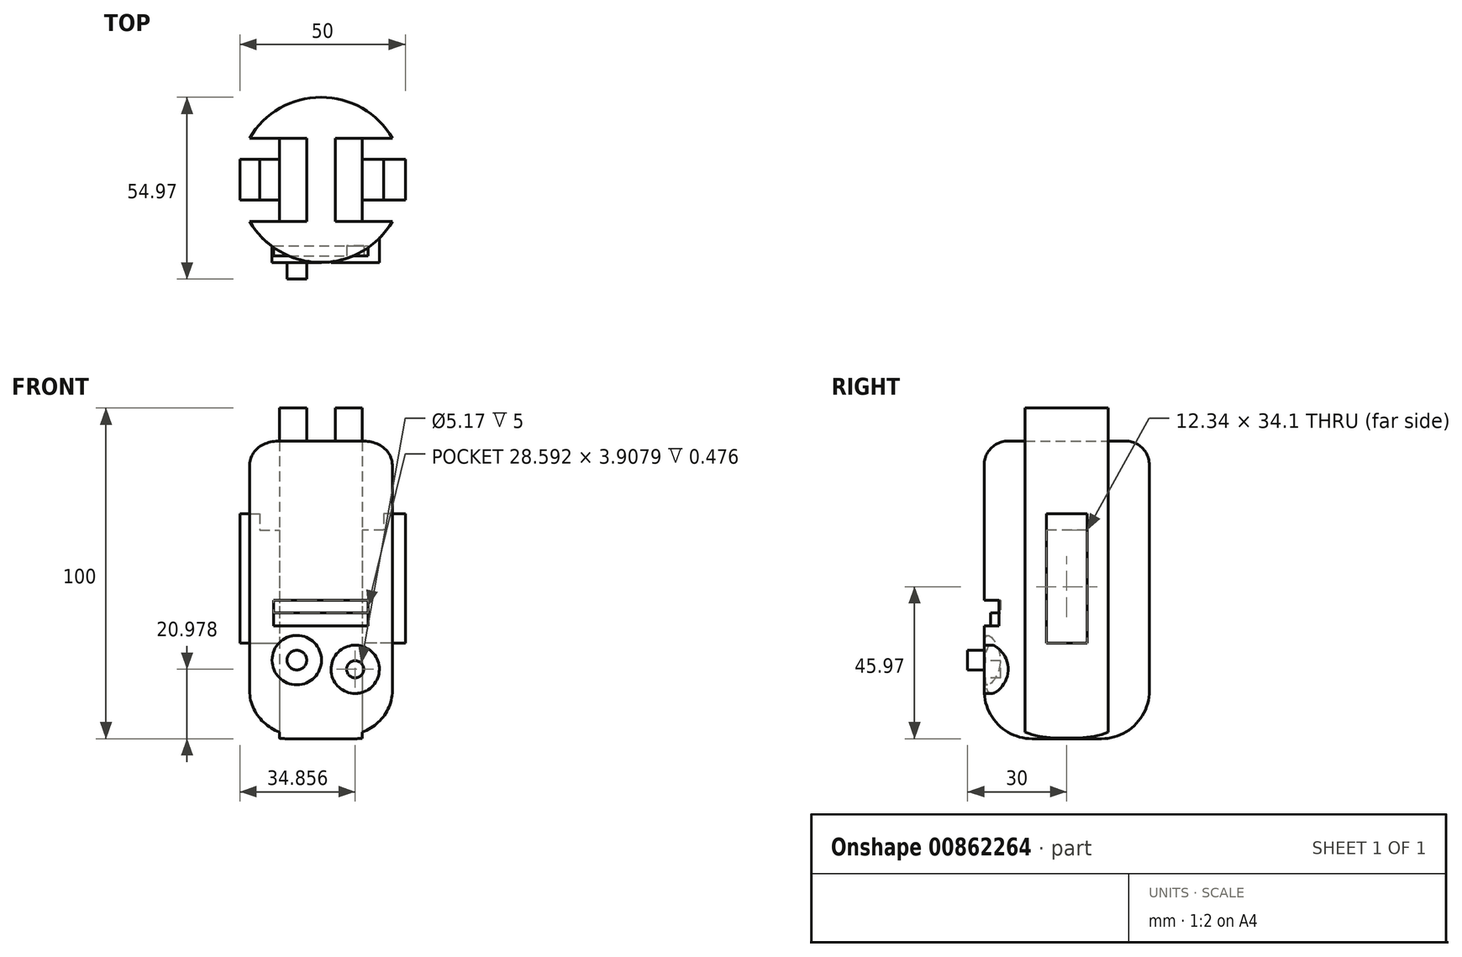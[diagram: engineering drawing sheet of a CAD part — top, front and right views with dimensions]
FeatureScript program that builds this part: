
annotation { "Feature Type Name" : "Feature", "Feature Type Description" : "" }
export const myFeature = defineFeature(function(context is Context, id is Id, definition is map)
    precondition{}
    {
        {
            var Q0;
            Q0=qCreatedBy(makeId("Top.planeOp"),FACE);
            var sketch = newSketch(context, id + "F0", { "sketchPlane" : qUnion([Q0])});
            skCircle(sketch, "E0", {"center": v(0, 0) * mm, "radius": 24.97 * mm});
            skSolve(sketch);
        }
        {
            var Q0;
            Q0=makeQuery(id+"F0.imprint","IMPRINT",FACE,{"disambiguationData":[TD([[makeQuery(id+"F0.imprint","IMPRINT",EDGE,{"derivedFrom":sQuery(id+"F0.wireOp",EDGE,"E0")}),1.0]])]});
            extrude(context, id + "F1", {"entities" : qUnion([Q0]), "depth" : 80 * mm, "offsetDistance" : 25 * mm});
        }
        {
            var Q0;
            Q0=makeQuery(id+"F1.opExtrude","CAP_FACE",FACE,{"disambiguationData":[OSD([sQuery(id+"F0.wireOp",EDGE,"E0")])],"isStart":false});
            fillet(context, id + "F2", {"entities" : qUnion([Q0]), "radius" : 7.24 * mm, "tangentPropagation" : true, "allowEdgeOverflow" : false});
        }
        {
            var Q0;
            Q0=makeQuery(id+"F1.opExtrude","CAP_FACE",FACE,{"disambiguationData":[OSD([sQuery(id+"F0.wireOp",EDGE,"E0")])],"isStart":false});
            var sketch = newSketch(context, id + "F3", { "sketchPlane" : qUnion([Q0])});
            skLineSegment(sketch, "E1.bottom", {"start": v(12.5, -12.57) * mm, "end": v(-12.5, -12.57) * mm});
            skLineSegment(sketch, "E1.top", {"start": v(12.5, 12.57) * mm, "end": v(-12.5, 12.57) * mm});
            skLineSegment(sketch, "E1.left", {"start": v(12.5, -12.57) * mm, "end": v(12.5, 12.57) * mm});
            skLineSegment(sketch, "E1.right", {"start": v(-12.5, -12.57) * mm, "end": v(-12.5, 12.57) * mm});
            skPoint(sketch, "E1.middle", {"position": v(0, 0) * mm});
            skSolve(sketch);
        }
        {
            var Q0;
            Q0 = qSketchRegion(id + "F3", true);
            extrude(context, id + "F4", {"entities" : qUnion([Q0]), "operationType" : NewBodyOperationType.ADD, "depth" : 10 * mm, "offsetDistance" : 25 * mm});
        }
        {
            var Q0;
            Q0=makeQuery(id+"F4.opExtrude","CAP_FACE",FACE,{"disambiguationData":[OSD([sQuery(id+"F3.wireOp",EDGE,"E1.bottom"),sQuery(id+"F3.wireOp",EDGE,"E1.top"),sQuery(id+"F3.wireOp",EDGE,"E1.left"),sQuery(id+"F3.wireOp",EDGE,"E1.right")])],"isStart":false});
            var sketch = newSketch(context, id + "F5", { "sketchPlane" : qUnion([Q0])});
            skLineSegment(sketch, "E2.bottom", {"start": v(4.3, -21.17) * mm, "end": v(-4.3, -21.17) * mm});
            skLineSegment(sketch, "E2.top", {"start": v(4.3, 21.17) * mm, "end": v(-4.3, 21.17) * mm});
            skLineSegment(sketch, "E2.left", {"start": v(4.3, -21.17) * mm, "end": v(4.3, 21.17) * mm});
            skLineSegment(sketch, "E2.right", {"start": v(-4.3, -21.17) * mm, "end": v(-4.3, 21.17) * mm});
            skPoint(sketch, "E2.middle", {"position": v(0, 0) * mm});
            skSolve(sketch);
        }
        {
            var Q0;
            Q0 = qSketchRegion(id + "F5", true);
            extrude(context, id + "F6", {"entities" : qUnion([Q0]), "operationType" : NewBodyOperationType.REMOVE, "oppositeDirection" : true, "depth" : 10 * mm, "offsetDistance" : 25 * mm});
        }
        {
            var Q0;
            Q0=makeQuery(id+"F1.opExtrude","CAP_FACE",FACE,{"disambiguationData":[OSD([sQuery(id+"F0.wireOp",EDGE,"E0")])],"isStart":true});
            var sketch = newSketch(context, id + "F7", { "sketchPlane" : qUnion([Q0])});
            skCircle(sketch, "E3", {"center": v(0, 0) * mm, "radius": 24.97 * mm});
            skSolve(sketch);
        }
        {
            var Q0;
            Q0 = qSketchRegion(id + "F7", true);
            extrude(context, id + "F8", {"entities" : qUnion([Q0]), "operationType" : NewBodyOperationType.ADD, "depth" : 10 * mm, "offsetDistance" : 25 * mm});
        }
        {
            var Q0;
            Q0=makeQuery(id+"F8.opExtrude","CAP_EDGE",EDGE,{"disambiguationData":[OSD([sQuery(id+"F7.wireOp",EDGE,"E3")])],"isStart":false});
            fillet(context, id + "F9", {"entities" : qUnion([Q0]), "radius" : 14.5 * mm, "tangentPropagation" : true, "allowEdgeOverflow" : false});
        }
        {
            var Q0;
            Q0=qCreatedBy(makeId("Front.planeOp"),FACE);
            var sketch = newSketch(context, id + "F10", { "sketchPlane" : qUnion([Q0])});
            skCircle(sketch, "E4", {"center": v(10.36, 10.98) * mm, "radius": 7.3 * mm});
            skCircle(sketch, "E5", {"center": v(-7.3, 13.75) * mm, "radius": 7.48 * mm});
            skSolve(sketch);
        }
        {
            var Q0;
            Q0=sQuery(id+"F10.wireOp",EDGE,"E5");
            extrude(context, id + "F11", {"bodyType" : ToolBodyType.SURFACE, "surfaceEntities" : qUnion([Q0]), "depth" : 25 * mm, "offsetDistance" : 25 * mm});
        }
        {
            var Q0;
            Q0 = qSketchRegion(id + "F10", true);
            extrude(context, id + "F12", {"entities" : qUnion([Q0]), "operationType" : NewBodyOperationType.ADD, "depth" : 25 * mm, "offsetDistance" : 25 * mm});
        }
        {
            var Q0;
            Q0=makeQuery(id+"F12.opExtrude","CAP_FACE",FACE,{"disambiguationData":[OSD([sQuery(id+"F10.wireOp",EDGE,"E4")])],"isStart":false});
            var sketch = newSketch(context, id + "F13", { "sketchPlane" : qUnion([Q0])});
            skCircle(sketch, "E6", {"center": v(10.36, 10.98) * mm, "radius": 2.58 * mm});
            skSolve(sketch);
        }
        {
            var Q0;
            Q0=makeQuery(id+"F13.imprint","IMPRINT",FACE,{"disambiguationData":[TD([[makeQuery(id+"F13.imprint","IMPRINT",EDGE,{"derivedFrom":sQuery(id+"F13.wireOp",EDGE,"E6")}),1.0]])]});
            extrude(context, id + "F14", {"entities" : qUnion([Q0]), "operationType" : NewBodyOperationType.REMOVE, "oppositeDirection" : true, "depth" : 5 * mm, "offsetDistance" : 25 * mm});
        }
        {
            var Q0;
            Q0=makeQuery(id+"F12.opExtrude","CAP_FACE",FACE,{"disambiguationData":[OSD([sQuery(id+"F10.wireOp",EDGE,"E5")])],"isStart":false});
            var sketch = newSketch(context, id + "F15", { "sketchPlane" : qUnion([Q0])});
            skCircle(sketch, "E7", {"center": v(-7.3, 13.75) * mm, "radius": 2.98 * mm});
            skSolve(sketch);
        }
        {
            var Q0;
            Q0=makeQuery(id+"F15.imprint","IMPRINT",FACE,{"disambiguationData":[TD([[makeQuery(id+"F15.imprint","IMPRINT",EDGE,{"derivedFrom":sQuery(id+"F15.wireOp",EDGE,"E7")}),1.0]])]});
            extrude(context, id + "F16", {"entities" : qUnion([Q0]), "operationType" : NewBodyOperationType.ADD, "depth" : 5 * mm, "offsetDistance" : 25 * mm});
        }
        {
            var Q0;
            Q0=makeQuery(id+"F12.opExtrude","CAP_FACE",FACE,{"disambiguationData":[OSD([sQuery(id+"F10.wireOp",EDGE,"E4")])],"isStart":false});
            var sketch = newSketch(context, id + "F17", { "sketchPlane" : qUnion([Q0])});
            skLineSegment(sketch, "E8.bottom", {"start": v(-14.3, 31.9) * mm, "end": v(14.3, 31.9) * mm});
            skLineSegment(sketch, "E8.top", {"start": v(-14.3, 24.08) * mm, "end": v(14.3, 24.08) * mm});
            skLineSegment(sketch, "E8.left", {"start": v(-14.3, 31.9) * mm, "end": v(-14.3, 24.08) * mm});
            skLineSegment(sketch, "E8.right", {"start": v(14.3, 31.9) * mm, "end": v(14.3, 24.08) * mm});
            skPoint(sketch, "E8.middle", {"position": v(0, 27.99) * mm});
            skSolve(sketch);
        }
        {
            var Q0;
            Q0=makeQuery(id+"F17.imprint","IMPRINT",FACE,{"disambiguationData":[TD([[makeQuery(id+"F17.imprint","IMPRINT",EDGE,{"derivedFrom":sQuery(id+"F17.wireOp",EDGE,"E8.bottom")}),-1.0]])]});
            extrude(context, id + "F18", {"entities" : qUnion([Q0]), "operationType" : NewBodyOperationType.REMOVE, "oppositeDirection" : true, "depth" : 5 * mm, "offsetDistance" : 25 * mm});
        }
        {
            var Q0;
            Q0=makeQuery(id+"F18.boolean.opBoolean","COPY",FACE,{"derivedFrom":makeQuery(id+"F18.opExtrude","CAP_FACE",FACE,{"disambiguationData":[OSD([sQuery(id+"F17.wireOp",EDGE,"E8.bottom"),sQuery(id+"F17.wireOp",EDGE,"E8.top"),sQuery(id+"F17.wireOp",EDGE,"E8.left"),sQuery(id+"F17.wireOp",EDGE,"E8.right")])],"isStart":false})});
            var sketch = newSketch(context, id + "F19", { "sketchPlane" : qUnion([Q0])});
            skLineSegment(sketch, "E9.bottom", {"start": v(14.3, 24.08) * mm, "end": v(-14.3, 24.08) * mm});
            skLineSegment(sketch, "E9.top", {"start": v(14.3, 27.99) * mm, "end": v(-14.3, 27.99) * mm});
            skLineSegment(sketch, "E9.left", {"start": v(14.3, 24.08) * mm, "end": v(14.3, 27.99) * mm});
            skLineSegment(sketch, "E9.right", {"start": v(-14.3, 24.08) * mm, "end": v(-14.3, 27.99) * mm});
            skSolve(sketch);
        }
        {
            var Q0;
            Q0=makeQuery(id+"F19.imprint","IMPRINT",FACE,{"disambiguationData":[TD([[makeQuery(id+"F19.imprint","IMPRINT",EDGE,{"derivedFrom":sQuery(id+"F19.wireOp",EDGE,"E9.bottom")}),1.0]])]});
            extrude(context, id + "F20", {"entities" : qUnion([Q0]), "operationType" : NewBodyOperationType.ADD, "depth" : 3 * mm, "offsetDistance" : 25 * mm});
        }
        {
            var Q0;
            Q0=makeQuery(id+"F4.opExtrude","SWEPT_FACE",FACE,{"disambiguationData":[OSD([sQuery(id+"F3.wireOp",EDGE,"E1.right")])]});
            var sketch = newSketch(context, id + "F21", { "sketchPlane" : qUnion([Q0])});
            skLineSegment(sketch, "E10.bottom", {"start": v(-12.57, 80) * mm, "end": v(12.57, 80) * mm});
            skLineSegment(sketch, "E10.top", {"start": v(-12.57, -80) * mm, "end": v(12.57, -80) * mm});
            skLineSegment(sketch, "E10.left", {"start": v(-12.57, 80) * mm, "end": v(-12.57, -80) * mm});
            skLineSegment(sketch, "E10.right", {"start": v(12.57, 80) * mm, "end": v(12.57, -80) * mm});
            skPoint(sketch, "E10.middle", {"position": v(0, 0) * mm});
            skSolve(sketch);
        }
        {
            var Q0;
            Q0=makeQuery(id+"F21.imprint","IMPRINT",FACE,{"disambiguationData":[TD([[makeQuery(id+"F21.imprint","IMPRINT",EDGE,{"derivedFrom":sQuery(id+"F21.wireOp",EDGE,"E10.bottom")}),1.0]])]});
            extrude(context, id + "F22", {"entities" : qUnion([Q0]), "operationType" : NewBodyOperationType.REMOVE, "depth" : 25 * mm, "offsetDistance" : 25 * mm});
        }
        {
            var Q0;
            Q0=makeQuery(id+"F4.opExtrude","SWEPT_FACE",FACE,{"disambiguationData":[OSD([sQuery(id+"F3.wireOp",EDGE,"E1.left")])]});
            var sketch = newSketch(context, id + "F23", { "sketchPlane" : qUnion([Q0])});
            skLineSegment(sketch, "E11.bottom", {"start": v(-12.57, 80) * mm, "end": v(12.57, 80) * mm});
            skLineSegment(sketch, "E11.top", {"start": v(-12.57, -80) * mm, "end": v(12.57, -80) * mm});
            skLineSegment(sketch, "E11.left", {"start": v(-12.57, 80) * mm, "end": v(-12.57, -80) * mm});
            skLineSegment(sketch, "E11.right", {"start": v(12.57, 80) * mm, "end": v(12.57, -80) * mm});
            skPoint(sketch, "E11.middle", {"position": v(0, 0) * mm});
            skSolve(sketch);
        }
        {
            var Q0;
            Q0=makeQuery(id+"F23.imprint","IMPRINT",FACE,{"disambiguationData":[TD([[makeQuery(id+"F23.imprint","IMPRINT",EDGE,{"derivedFrom":sQuery(id+"F23.wireOp",EDGE,"E11.bottom")}),-1.0]])]});
            extrude(context, id + "F24", {"entities" : qUnion([Q0]), "operationType" : NewBodyOperationType.REMOVE, "depth" : 25 * mm, "offsetDistance" : 25 * mm});
        }
        {
            var Q0;
            Q0=makeQuery(id+"F22.boolean.opBoolean","MERGE",FACE,{"derivedFrom":[makeQuery(id+"F4.opExtrude","SWEPT_FACE",FACE,{"disambiguationData":[OSD([sQuery(id+"F3.wireOp",EDGE,"E1.right")])]}),makeQuery(id+"F22.opExtrude","CAP_FACE",FACE,{"disambiguationData":[OSD([sQuery(id+"F21.wireOp",EDGE,"E10.bottom"),sQuery(id+"F21.wireOp",EDGE,"E10.top"),sQuery(id+"F21.wireOp",EDGE,"E10.left"),sQuery(id+"F21.wireOp",EDGE,"E10.right")])],"isStart":true})]});
            var sketch = newSketch(context, id + "F25", { "sketchPlane" : qUnion([Q0])});
            skLineSegment(sketch, "E12.bottom", {"start": v(-6.17, 53.02) * mm, "end": v(6.17, 53.02) * mm});
            skLineSegment(sketch, "E12.top", {"start": v(-6.17, 18.92) * mm, "end": v(6.17, 18.92) * mm});
            skLineSegment(sketch, "E12.left", {"start": v(-6.17, 53.02) * mm, "end": v(-6.17, 18.92) * mm});
            skLineSegment(sketch, "E12.right", {"start": v(6.17, 53.02) * mm, "end": v(6.17, 18.92) * mm});
            skPoint(sketch, "E12.middle", {"position": v(0, 35.97) * mm});
            skPoint(sketch, "E12.middle.positionSnap0", {"position": v(-12.57, 35.97) * mm});
            skPoint(sketch, "E12.centerSnap0", {"position": v(-12.57, 35.97) * mm});
            skSolve(sketch);
        }
        {
            var Q0;
            Q0=makeQuery(id+"F25.imprint","IMPRINT",FACE,{"disambiguationData":[TD([[makeQuery(id+"F25.imprint","IMPRINT",EDGE,{"derivedFrom":sQuery(id+"F25.wireOp",EDGE,"E12.bottom")}),-1.0]])]});
            extrude(context, id + "F26", {"entities" : qUnion([Q0]), "operationType" : NewBodyOperationType.ADD, "oppositeDirection" : true, "depth" : 38 * mm, "offsetDistance" : 25 * mm});
        }
        {
            var Q0;
            Q0 = qSketchRegion(id + "F25", true);
            extrude(context, id + "F27", {"entities" : qUnion([Q0]), "operationType" : NewBodyOperationType.ADD, "depth" : 12 * mm, "offsetDistance" : 25 * mm});
        }
        {
            var Q0;
            Q0=makeQuery(id+"F27.opExtrude","SWEPT_FACE",FACE,{"disambiguationData":[OSD([sQuery(id+"F25.wireOp",EDGE,"E12.bottom")])]});
            var sketch = newSketch(context, id + "F28", { "sketchPlane" : qUnion([Q0])});
            skLineSegment(sketch, "E13.bottom", {"start": v(-24.5, -6.17) * mm, "end": v(-18.5, -6.17) * mm});
            skLineSegment(sketch, "E13.top", {"start": v(-24.5, 6.17) * mm, "end": v(-18.5, 6.17) * mm});
            skLineSegment(sketch, "E13.left", {"start": v(-24.5, -6.17) * mm, "end": v(-24.5, 6.17) * mm});
            skLineSegment(sketch, "E13.right", {"start": v(-18.5, -6.17) * mm, "end": v(-18.5, 6.17) * mm});
            skSolve(sketch);
        }
        {
            var Q0;
            Q0=makeQuery(id+"F28.imprint","IMPRINT",FACE,{"disambiguationData":[TD([[makeQuery(id+"F28.imprint","IMPRINT",EDGE,{"derivedFrom":sQuery(id+"F28.wireOp",EDGE,"E13.bottom")}),1.0]])]});
            extrude(context, id + "F29", {"entities" : qUnion([Q0]), "operationType" : NewBodyOperationType.ADD, "depth" : 5 * mm, "offsetDistance" : 25 * mm});
        }
        {
            var Q0;
            Q0=makeQuery(id+"F26.opExtrude","SWEPT_FACE",FACE,{"disambiguationData":[OSD([sQuery(id+"F25.wireOp",EDGE,"E12.bottom")])]});
            var sketch = newSketch(context, id + "F30", { "sketchPlane" : qUnion([Q0])});
            skLineSegment(sketch, "E14.bottom", {"start": v(25.5, -6.17) * mm, "end": v(19, -6.17) * mm});
            skLineSegment(sketch, "E14.top", {"start": v(25.5, 6.17) * mm, "end": v(19, 6.17) * mm});
            skLineSegment(sketch, "E14.left", {"start": v(25.5, -6.17) * mm, "end": v(25.5, 6.17) * mm});
            skLineSegment(sketch, "E14.right", {"start": v(19, -6.17) * mm, "end": v(19, 6.17) * mm});
            skSolve(sketch);
        }
        {
            var Q0;
            Q0=makeQuery(id+"F30.imprint","IMPRINT",FACE,{"disambiguationData":[TD([[makeQuery(id+"F30.imprint","IMPRINT",EDGE,{"derivedFrom":sQuery(id+"F30.wireOp",EDGE,"E14.bottom")}),-1.0]])]});
            extrude(context, id + "F31", {"entities" : qUnion([Q0]), "operationType" : NewBodyOperationType.ADD, "depth" : 5 * mm, "offsetDistance" : 25 * mm});
        }
    });
